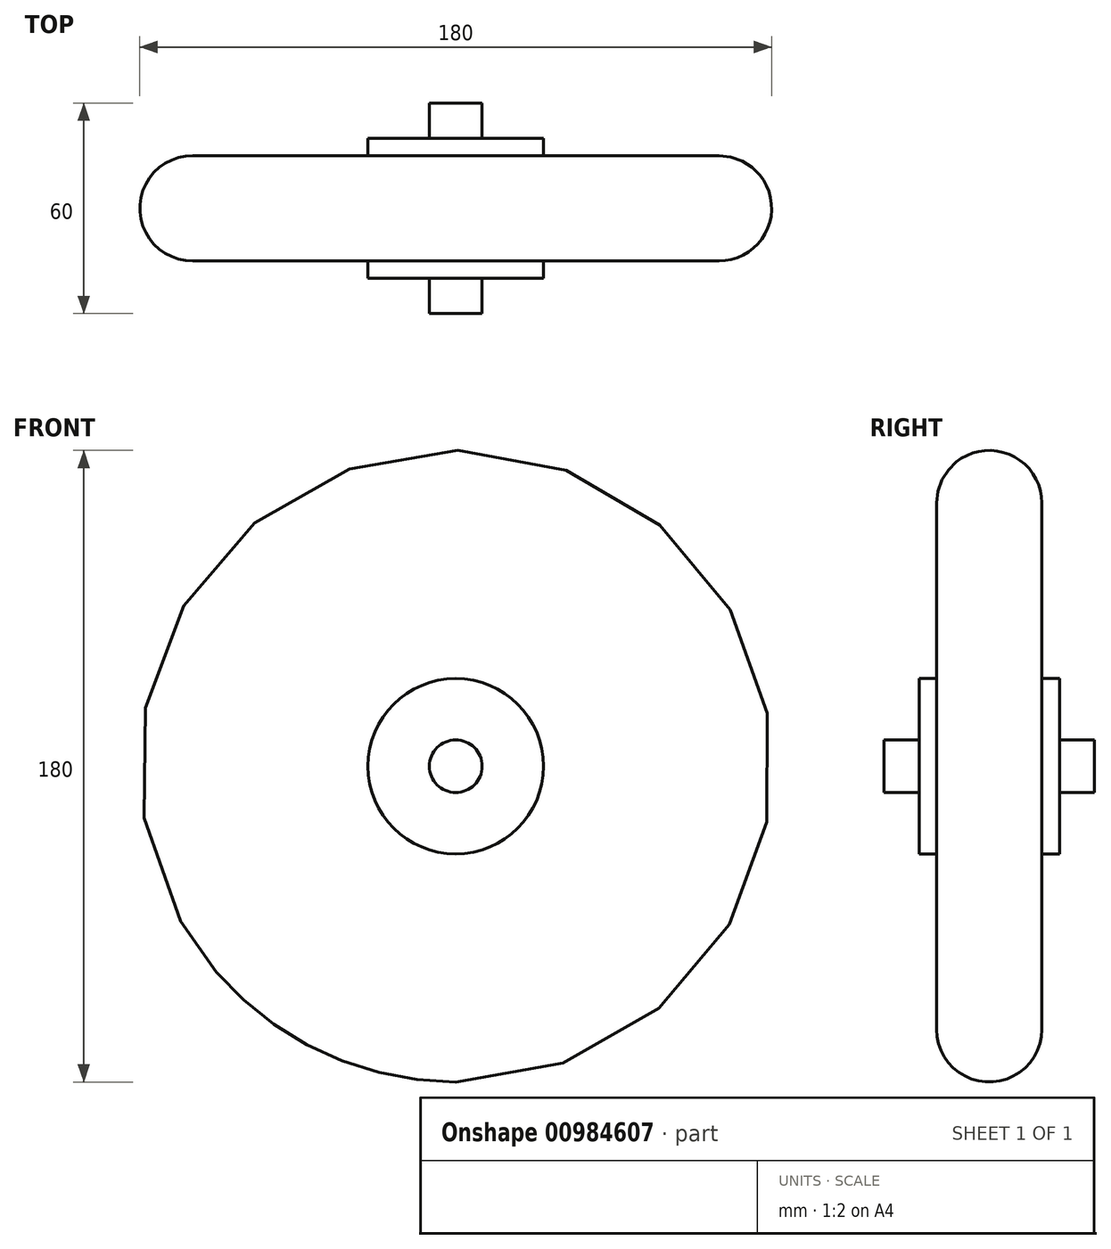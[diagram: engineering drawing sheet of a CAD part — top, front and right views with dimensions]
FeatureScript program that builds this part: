
annotation { "Feature Type Name" : "Feature", "Feature Type Description" : "" }
export const myFeature = defineFeature(function(context is Context, id is Id, definition is map)
    precondition{}
    {
        {
            var Q0;
            Q0=qCreatedBy(makeId("Front.planeOp"),FACE);
            var sketch = newSketch(context, id + "F0", { "sketchPlane" : qUnion([Q0])});
            skCircle(sketch, "E0", {"center": v(0, 0) * mm, "radius": 90 * mm});
            skCircle(sketch, "E1", {"center": v(0, 0) * mm, "radius": 25 * mm});
            skCircle(sketch, "E2", {"center": v(0, 0) * mm, "radius": 7.5 * mm});
            skSolve(sketch);
        }
        {
            var Q0;
            Q0=makeQuery(id+"F0.imprint","IMPRINT",FACE,{"disambiguationData":[TD([[makeQuery(id+"F0.imprint","IMPRINT",EDGE,{"derivedFrom":sQuery(id+"F0.wireOp",EDGE,"E0")}),1.0]])]});
            extrude(context, id + "F1", {"entities" : qUnion([Q0]), "depth" : 30 * mm, "offsetDistance" : 25 * mm});
        }
        {
            var Q0;
            Q0=makeQuery(id+"F0.imprint","IMPRINT",FACE,{"disambiguationData":[TD([[makeQuery(id+"F0.imprint","IMPRINT",EDGE,{"derivedFrom":sQuery(id+"F0.wireOp",EDGE,"E1")}),1.0]])]});
            extrude(context, id + "F2", {"entities" : qUnion([Q0]), "operationType" : NewBodyOperationType.ADD, "depth" : 35 * mm, "offsetDistance" : 25 * mm});
        }
        {
            var Q0;
            Q0=makeQuery(id+"F1.opExtrude","CAP_EDGE",EDGE,{"disambiguationData":[OSD([sQuery(id+"F0.wireOp",EDGE,"E0")])],"isStart":false});
            var Q1;
            Q1=makeQuery(id+"F1.opExtrude","CAP_EDGE",EDGE,{"disambiguationData":[OSD([sQuery(id+"F0.wireOp",EDGE,"E0")])],"isStart":true});
            fillet(context, id + "F3", {"entities" : qUnion([Q0, Q1]), "radius" : 15 * mm, "tangentPropagation" : true, "allowEdgeOverflow" : false});
        }
        {
            var Q0;
            Q0=makeQuery(id+"F0.imprint","IMPRINT",FACE,{"disambiguationData":[TD([[makeQuery(id+"F0.imprint","IMPRINT",EDGE,{"derivedFrom":sQuery(id+"F0.wireOp",EDGE,"E1")}),1.0]])]});
            extrude(context, id + "F4", {"entities" : qUnion([Q0]), "operationType" : NewBodyOperationType.ADD, "oppositeDirection" : true, "depth" : 5 * mm, "offsetDistance" : 25 * mm});
        }
        {
            var Q0;
            Q0=makeQuery(id+"F0.imprint","IMPRINT",FACE,{"disambiguationData":[TD([[makeQuery(id+"F0.imprint","IMPRINT",EDGE,{"derivedFrom":sQuery(id+"F0.wireOp",EDGE,"E2")}),1.0]])]});
            extrude(context, id + "F5", {"entities" : qUnion([Q0]), "operationType" : NewBodyOperationType.ADD, "oppositeDirection" : true, "depth" : 15 * mm, "offsetDistance" : 25 * mm, "hasSecondDirection" : true, "secondDirectionOppositeDirection" : false, "secondDirectionDepth" : 45 * mm});
        }
    });
